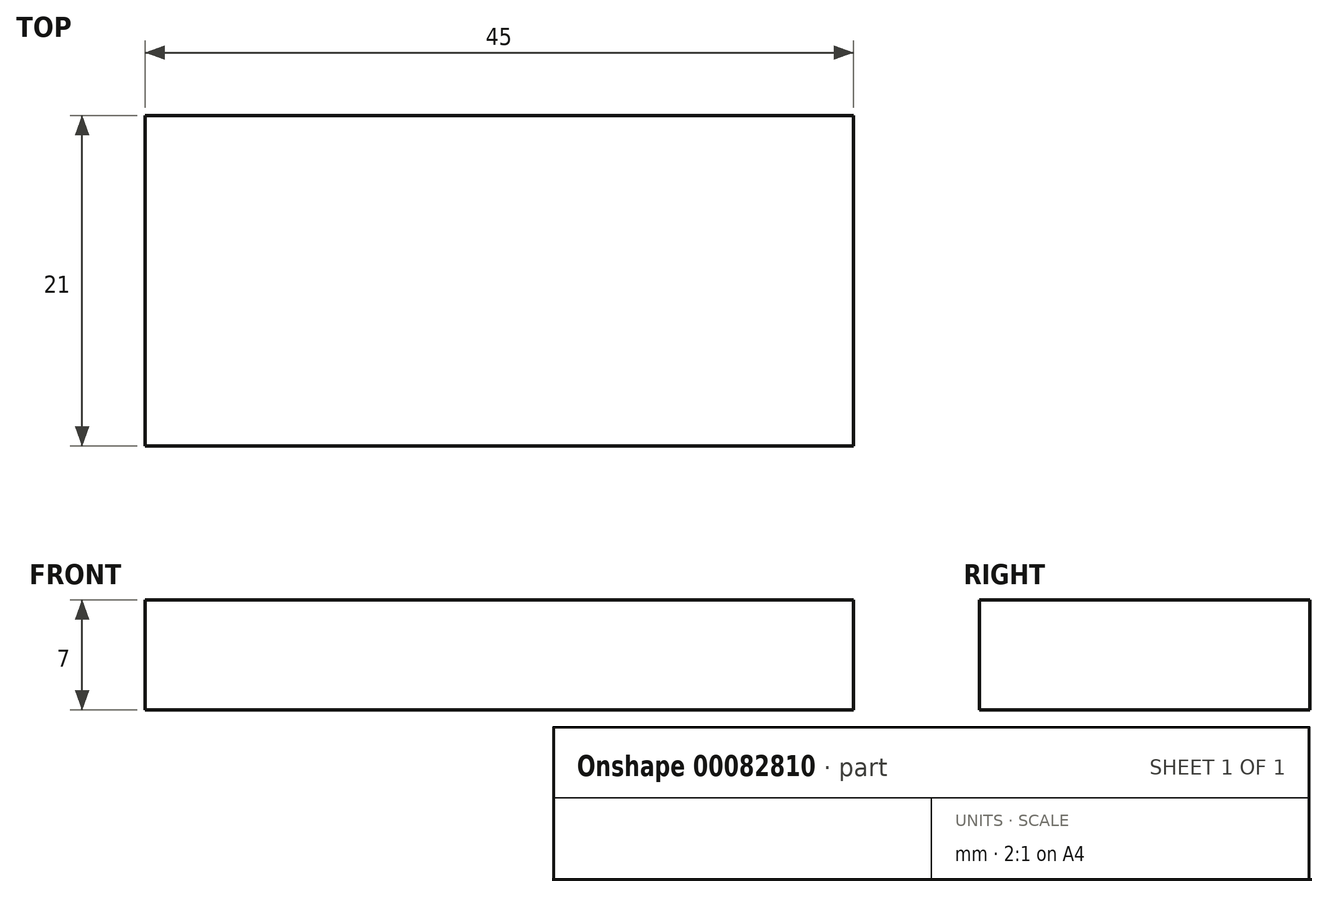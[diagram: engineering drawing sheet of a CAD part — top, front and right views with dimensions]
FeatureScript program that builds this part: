
annotation { "Feature Type Name" : "Feature", "Feature Type Description" : "" }
export const myFeature = defineFeature(function(context is Context, id is Id, definition is map)
    precondition{}
    {
        {
            var Q0;
            Q0=qCreatedBy(makeId("Top.planeOp"),FACE);
            var sketch = newSketch(context, id + "F0", { "sketchPlane" : qUnion([Q0])});
            skLineSegment(sketch, "E0.bottom", {"start": v(22.5, 10.5) * mm, "end": v(-22.5, 10.5) * mm});
            skLineSegment(sketch, "E0.top", {"start": v(22.5, -10.5) * mm, "end": v(-22.5, -10.5) * mm});
            skLineSegment(sketch, "E0.left", {"start": v(22.5, 10.5) * mm, "end": v(22.5, -10.5) * mm});
            skLineSegment(sketch, "E0.right", {"start": v(-22.5, 10.5) * mm, "end": v(-22.5, -10.5) * mm});
            skPoint(sketch, "E0.middle", {"position": v(0, 0) * mm});
            skSolve(sketch);
        }
        {
            var Q0;
            Q0 = qSketchRegion(id + "F0", true);
            extrude(context, id + "F1", {"entities" : qUnion([Q0]), "depth" : 7 * mm});
        }
    });
